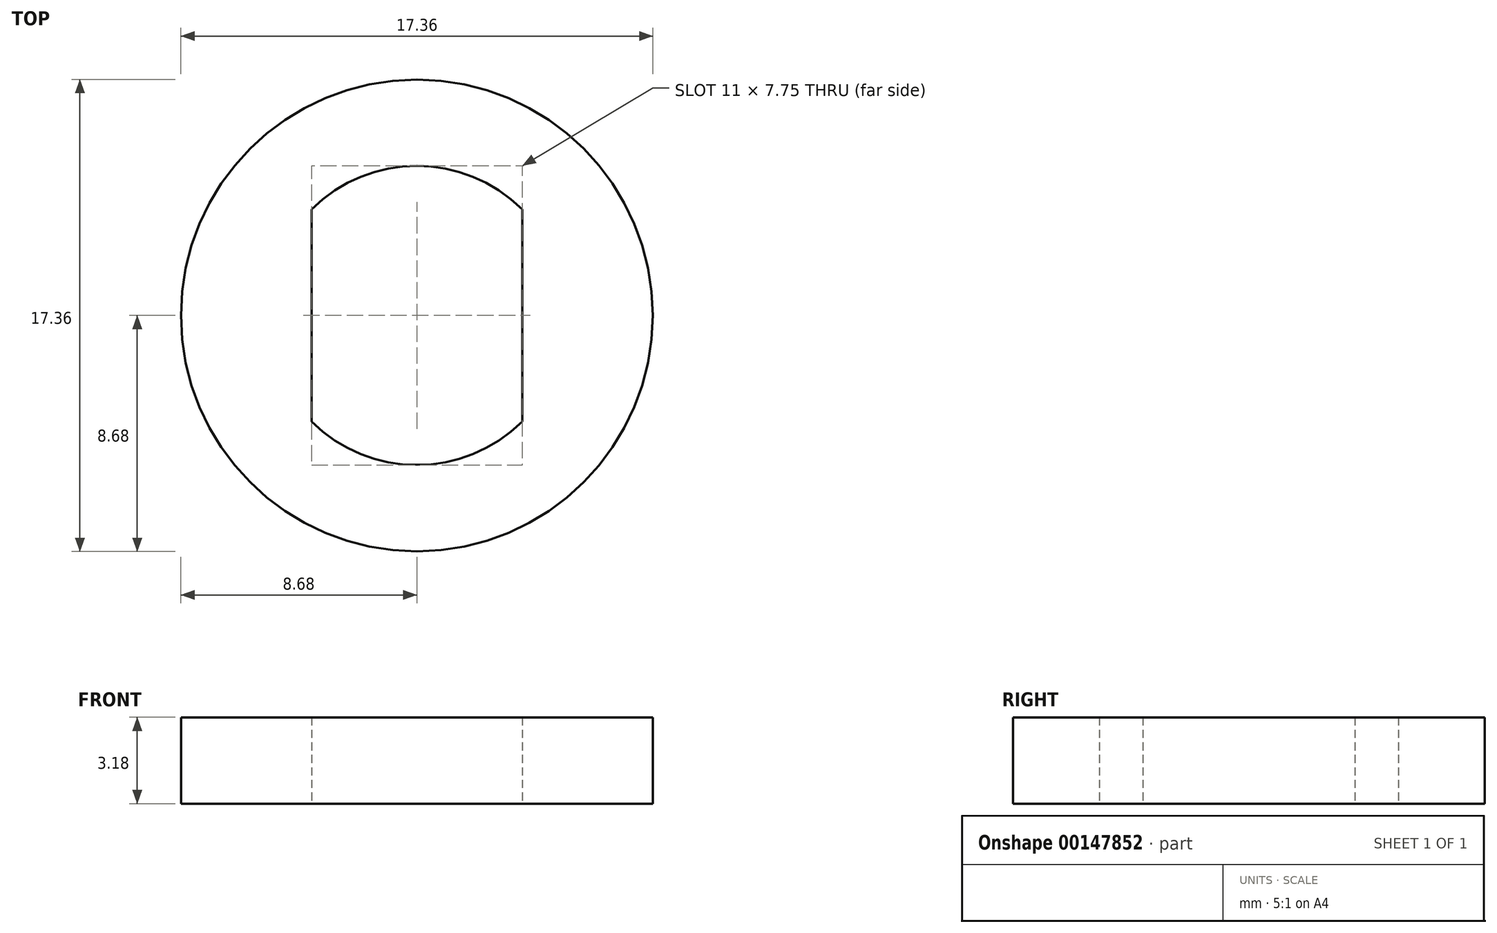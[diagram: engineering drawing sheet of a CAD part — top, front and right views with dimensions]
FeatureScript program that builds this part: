
annotation { "Feature Type Name" : "Feature", "Feature Type Description" : "" }
export const myFeature = defineFeature(function(context is Context, id is Id, definition is map)
    precondition{}
    {
        {
            var Q0;
            Q0=qCreatedBy(makeId("Top.planeOp"),FACE);
            var sketch = newSketch(context, id + "F0", { "sketchPlane" : qUnion([Q0])});
            skLineSegment(sketch, "E0.bottom", {"start": v(-3.87, -3.9) * mm, "end": v(3.87, -3.9) * mm, "construction": true});
            skLineSegment(sketch, "E0.top", {"start": v(-3.87, 3.9) * mm, "end": v(3.87, 3.9) * mm, "construction": true});
            skLineSegment(sketch, "E0.left", {"start": v(-3.87, -3.9) * mm, "end": v(-3.87, 3.9) * mm});
            skLineSegment(sketch, "E0.right", {"start": v(3.87, -3.9) * mm, "end": v(3.87, 3.9) * mm});
            skPoint(sketch, "E0.middle", {"position": v(0, 0) * mm});
            skArc(sketch, "E1", {"start": v(3.87, 3.9) * mm, "mid": v(0, 5.5) * mm, "end": v(-3.87, 3.9) * mm});
            skArc(sketch, "E2", {"start": v(-3.87, -3.9) * mm, "mid": v(0, -5.5) * mm, "end": v(3.87, -3.9) * mm});
            skCircle(sketch, "E3", {"center": v(0, 0) * mm, "radius": 8.68 * mm});
            skSolve(sketch);
        }
        {
            var Q0;
            Q0=makeQuery(id+"F0.imprint","IMPRINT",FACE,{"disambiguationData":[TD([[makeQuery(id+"F0.imprint","IMPRINT",EDGE,{"derivedFrom":sQuery(id+"F0.wireOp",EDGE,"E0.left")}),1.0]])]});
            extrude(context, id + "F1", {"entities" : qUnion([Q0]), "depth" : 3.17 * mm});
        }
    });
